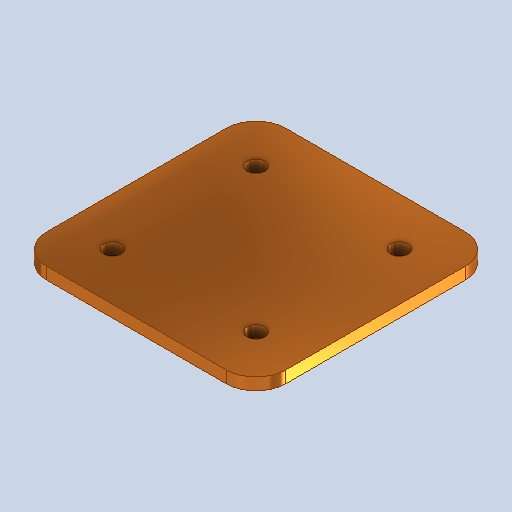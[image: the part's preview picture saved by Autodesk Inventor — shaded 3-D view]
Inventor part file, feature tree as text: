
AUTODESK INVENTOR PART (.ipt)
format: ipt  version: 2025.1 (Build 291241000, 241)  size: 243,200 bytes
history: native  units: mm
features: sketch x1, extrude x1, hole x1, fillet x1
ambient origin geometry x8: Origin, YZ Plane, XZ Plane, XY Plane, X Axis, Y Axis, Z Axis, Center Point
bodies: Solid1 (feature_tree)
feature tree (4):
  sketch  "Sketch1"  dims[d0=40.0mm d1=40.0mm d2=24.0mm d3=24.0mm d4=2.0mm d5=0.0mm d6=3.0mm d7=16.0mm d8=4.0mm d9=2.0mm d10=90.0deg d11=8.0mm d12=0.0mm d13=5.0mm]
  extrude  "Extrusion1"  Depth=40.0mm
  hole  "Hole1"  [1 undecoded]
  fillet  "Fillet1"  Radius=24.0mm
note: 1 required parameter value undecoded (feature->parameter linkage not recoverable at this tier; creation-order binding heuristic only, values carry confidence <= 0.55)
